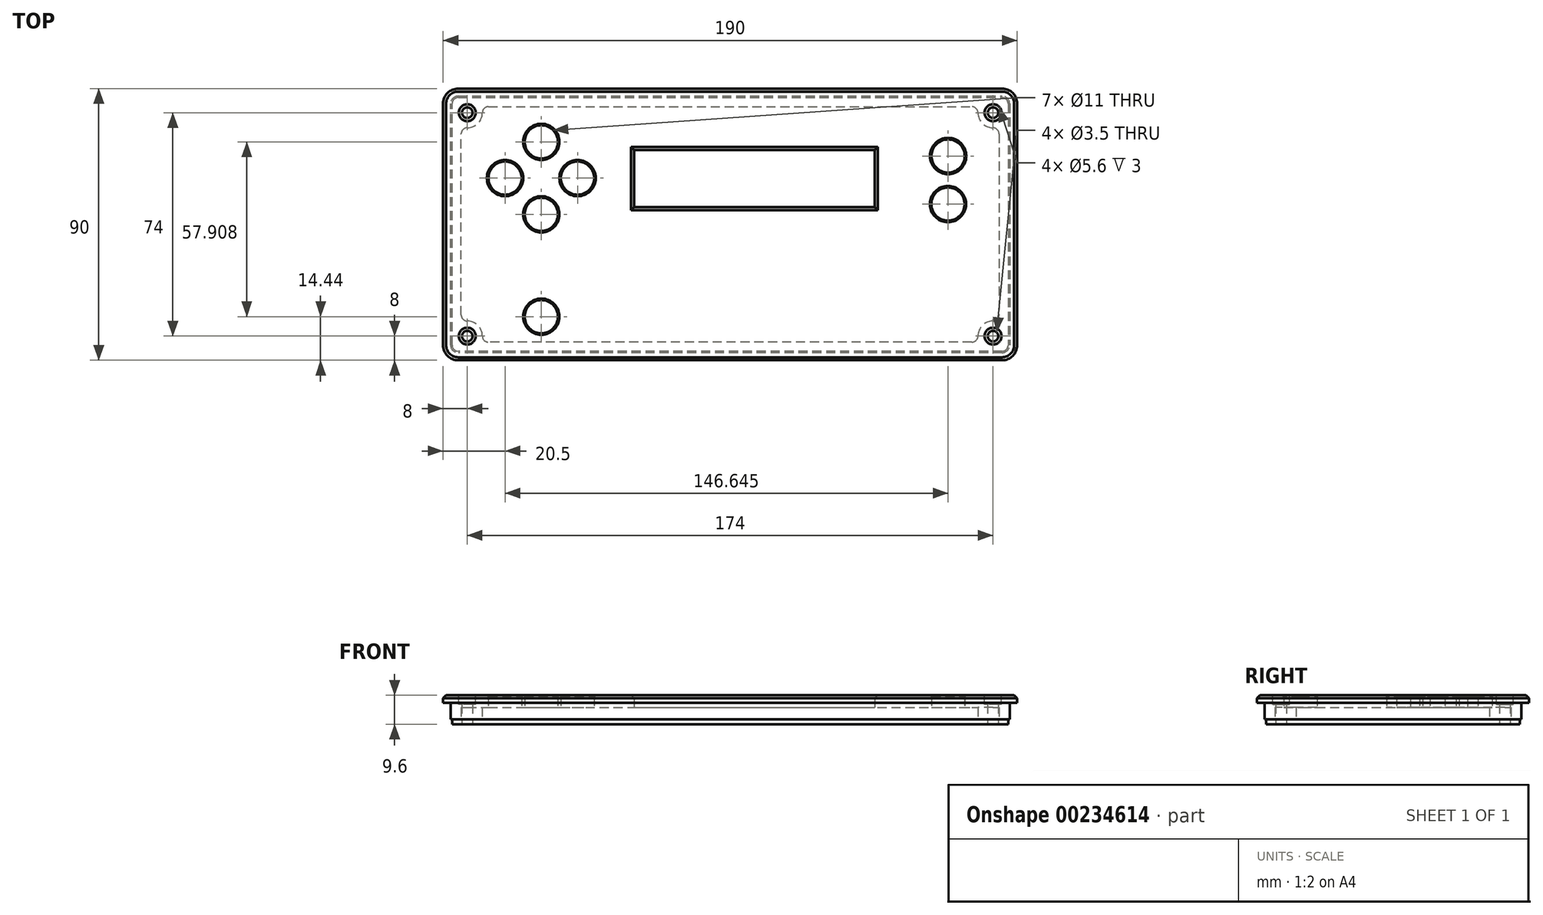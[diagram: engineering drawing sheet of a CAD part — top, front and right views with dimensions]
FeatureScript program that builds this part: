
annotation { "Feature Type Name" : "Feature", "Feature Type Description" : "" }
export const myFeature = defineFeature(function(context is Context, id is Id, definition is map)
    precondition{}
    {
        {
            var Q0;
            Q0=qCreatedBy(makeId("Top.planeOp"),FACE);
            var sketch = newSketch(context, id + "F0", { "sketchPlane" : qUnion([Q0])});
            skLineSegment(sketch, "E0.bottom", {"start": v(95, 45) * mm, "end": v(-95, 45) * mm});
            skLineSegment(sketch, "E0.top", {"start": v(95, -45) * mm, "end": v(-95, -45) * mm});
            skLineSegment(sketch, "E0.left", {"start": v(95, 45) * mm, "end": v(95, -45) * mm});
            skLineSegment(sketch, "E0.right", {"start": v(-95, 45) * mm, "end": v(-95, -45) * mm});
            skPoint(sketch, "E0.middle", {"position": v(0, 0) * mm});
            skCircle(sketch, "E1", {"center": v(-87, 37) * mm, "radius": 1.75 * mm});
            skLineSegment(sketch, "E2.bottom", {"start": v(47.83, 24.69) * mm, "end": v(-31.82, 24.69) * mm});
            skLineSegment(sketch, "E2.top", {"start": v(47.83, 5.74) * mm, "end": v(-31.82, 5.74) * mm});
            skLineSegment(sketch, "E2.left", {"start": v(47.83, 24.69) * mm, "end": v(47.83, 5.74) * mm});
            skLineSegment(sketch, "E2.right", {"start": v(-31.82, 24.69) * mm, "end": v(-31.82, 5.74) * mm});
            skCircle(sketch, "E3", {"center": v(-62.5, 27.35) * mm, "radius": 5.5 * mm});
            skCircle(sketch, "E4", {"center": v(-74.5, 15.35) * mm, "radius": 5.5 * mm});
            skCircle(sketch, "E5", {"center": v(-62.5, -30.56) * mm, "radius": 5.5 * mm});
            skCircle(sketch, "E6", {"center": v(72.14, 22.67) * mm, "radius": 5.5 * mm});
            skCircle(sketch, "E7", {"center": v(72.1, 6.74) * mm, "radius": 5.5 * mm});
            skLineSegment(sketch, "E8", {"start": v(-62.5, 27.35) * mm, "end": v(-62.5, -39.93) * mm, "construction": true});
            skLineSegment(sketch, "E9", {"start": v(-74.5, 15.35) * mm, "end": v(-45.37, 15.35) * mm, "construction": true});
            skCircle(sketch, "E10.MirrorC", {"center": v(-62.5, 3.35) * mm, "radius": 5.5 * mm});
            skCircle(sketch, "E11.MirrorC", {"center": v(-50.5, 15.35) * mm, "radius": 5.5 * mm});
            skLineSegment(sketch, "E12", {"start": v(72.14, 22.67) * mm, "end": v(72.1, 6.74) * mm, "construction": true});
            skCircle(sketch, "E13.MirrorC", {"center": v(87, 37) * mm, "radius": 1.75 * mm});
            skCircle(sketch, "E14.MirrorC", {"center": v(-87, -37) * mm, "radius": 1.75 * mm});
            skCircle(sketch, "E15.MirrorC", {"center": v(87, -37) * mm, "radius": 1.75 * mm});
            skSolve(sketch);
        }
        {
            var Q0;
            Q0 = qSketchRegion(id + "F0", true);
            extrude(context, id + "F1", {"entities" : qUnion([Q0]), "depth" : 8 * mm});
        }
        {
            var Q0;
            Q0=makeQuery(id+"F1.opExtrude","SWEPT_EDGE",EDGE,{"disambiguationData":[OSD([sQuery(id+"F0.wireOp",EDGE,"E0.bottom"),sQuery(id+"F0.wireOp",EDGE,"E0.right")])]});
            var Q1;
            Q1=makeQuery(id+"F1.opExtrude","SWEPT_EDGE",EDGE,{"disambiguationData":[OSD([sQuery(id+"F0.wireOp",EDGE,"E0.top"),sQuery(id+"F0.wireOp",EDGE,"E0.right")])]});
            var Q2;
            Q2=makeQuery(id+"F1.opExtrude","SWEPT_EDGE",EDGE,{"disambiguationData":[OSD([sQuery(id+"F0.wireOp",EDGE,"E0.top"),sQuery(id+"F0.wireOp",EDGE,"E0.left")])]});
            var Q3;
            Q3=makeQuery(id+"F1.opExtrude","SWEPT_EDGE",EDGE,{"disambiguationData":[OSD([sQuery(id+"F0.wireOp",EDGE,"E0.bottom"),sQuery(id+"F0.wireOp",EDGE,"E0.left")])]});
            fillet(context, id + "F2", {"entities" : qUnion([Q0, Q1, Q2, Q3]), "radius" : 5 * mm, "tangentPropagation" : true, "allowEdgeOverflow" : false});
        }
        {
            var Q0;
            Q0=makeQuery(id+"F1.opExtrude","CAP_FACE",FACE,{"disambiguationData":[OSD([sQuery(id+"F0.wireOp",EDGE,"E0.bottom"),sQuery(id+"F0.wireOp",EDGE,"E0.top"),sQuery(id+"F0.wireOp",EDGE,"E0.left"),sQuery(id+"F0.wireOp",EDGE,"E0.right"),sQuery(id+"F0.wireOp",EDGE,"E1"),sQuery(id+"F0.wireOp",EDGE,"E2.bottom"),sQuery(id+"F0.wireOp",EDGE,"E2.top"),sQuery(id+"F0.wireOp",EDGE,"E2.left"),sQuery(id+"F0.wireOp",EDGE,"E2.right"),sQuery(id+"F0.wireOp",EDGE,"E3"),sQuery(id+"F0.wireOp",EDGE,"E4"),sQuery(id+"F0.wireOp",EDGE,"E5"),sQuery(id+"F0.wireOp",EDGE,"E6"),sQuery(id+"F0.wireOp",EDGE,"E7"),sQuery(id+"F0.wireOp",EDGE,"E10.MirrorC"),sQuery(id+"F0.wireOp",EDGE,"E11.MirrorC"),sQuery(id+"F0.wireOp",EDGE,"E13.MirrorC"),sQuery(id+"F0.wireOp",EDGE,"E14.MirrorC"),sQuery(id+"F0.wireOp",EDGE,"E15.MirrorC")])],"isStart":true});
            var sketch = newSketch(context, id + "F3", { "sketchPlane" : qUnion([Q0])});
            skLineSegment(sketch, "E16.0", {"start": v(89, -32.42) * mm, "end": v(89, 32.42) * mm});
            skLineSegment(sketch, "E16.1", {"start": v(-82.42, -39) * mm, "end": v(82.42, -39) * mm});
            skLineSegment(sketch, "E16.3", {"start": v(82.42, 39) * mm, "end": v(-82.42, 39) * mm});
            skLineSegment(sketch, "E17.trimOffspring", {"start": v(-89, 32.42) * mm, "end": v(-89, -32.42) * mm});
            skArc(sketch, "E18", {"start": v(-89, 32.42) * mm, "mid": v(-83.46, 33.46) * mm, "end": v(-82.42, 39) * mm});
            skArc(sketch, "E19.MirrorC", {"start": v(89, 32.42) * mm, "mid": v(83.46, 33.46) * mm, "end": v(82.42, 39) * mm});
            skArc(sketch, "E20.MirrorC", {"start": v(-89, -32.42) * mm, "mid": v(-83.46, -33.46) * mm, "end": v(-82.42, -39) * mm});
            skArc(sketch, "E21.MirrorC", {"start": v(89, -32.42) * mm, "mid": v(83.46, -33.46) * mm, "end": v(82.42, -39) * mm});
            skPoint(sketch, "E22.orphan", {"position": v(-85.53, -39) * mm});
            skPoint(sketch, "E23.orphan", {"position": v(-89, -35.53) * mm});
            skPoint(sketch, "E24.orphan", {"position": v(-89, 35.53) * mm});
            skPoint(sketch, "E25.orphan", {"position": v(-85.53, 39) * mm});
            skPoint(sketch, "E26.orphan", {"position": v(89, 35.53) * mm});
            skPoint(sketch, "E27.orphan", {"position": v(85.53, 39) * mm});
            skPoint(sketch, "E28.orphan", {"position": v(89, -35.53) * mm});
            skPoint(sketch, "E29.orphan", {"position": v(85.53, -39) * mm});
            skSolve(sketch);
        }
        {
            var Q0;
            Q0 = qSketchRegion(id + "F3", true);
            extrude(context, id + "F4", {"entities" : qUnion([Q0]), "operationType" : NewBodyOperationType.REMOVE, "oppositeDirection" : true, "depth" : 4 * mm});
        }
        {
            var Q0;
            Q0=makeQuery(id+"F1.opExtrude","CAP_EDGE",EDGE,{"disambiguationData":[OSD([sQuery(id+"F0.wireOp",EDGE,"E3")])],"isStart":false});
            var Q1;
            Q1=makeQuery(id+"F1.opExtrude","CAP_EDGE",EDGE,{"disambiguationData":[OSD([sQuery(id+"F0.wireOp",EDGE,"E11.MirrorC")])],"isStart":false});
            var Q2;
            Q2=makeQuery(id+"F1.opExtrude","CAP_EDGE",EDGE,{"disambiguationData":[OSD([sQuery(id+"F0.wireOp",EDGE,"E4")])],"isStart":false});
            var Q3;
            Q3=makeQuery(id+"F1.opExtrude","CAP_EDGE",EDGE,{"disambiguationData":[OSD([sQuery(id+"F0.wireOp",EDGE,"E10.MirrorC")])],"isStart":false});
            var Q4;
            Q4=makeQuery(id+"F1.opExtrude","CAP_EDGE",EDGE,{"disambiguationData":[OSD([sQuery(id+"F0.wireOp",EDGE,"E5")])],"isStart":false});
            var Q5;
            Q5=makeQuery(id+"F1.opExtrude","CAP_EDGE",EDGE,{"disambiguationData":[OSD([sQuery(id+"F0.wireOp",EDGE,"E6")])],"isStart":false});
            var Q6;
            Q6=makeQuery(id+"F1.opExtrude","CAP_EDGE",EDGE,{"disambiguationData":[OSD([sQuery(id+"F0.wireOp",EDGE,"E7")])],"isStart":false});
            chamfer(context, id + "F5", {"entities" : qUnion([Q0, Q1, Q2, Q3, Q4, Q5, Q6]), "width" : .5 * mm, "tangentPropagation" : true});
        }
        {
            var Q0;
            Q0=makeQuery(id+"F1.opExtrude","CAP_EDGE",EDGE,{"disambiguationData":[OSD([sQuery(id+"F0.wireOp",EDGE,"E2.bottom")])],"isStart":false});
            var Q1;
            Q1=makeQuery(id+"F1.opExtrude","CAP_EDGE",EDGE,{"disambiguationData":[OSD([sQuery(id+"F0.wireOp",EDGE,"E2.right")])],"isStart":false});
            var Q2;
            Q2=makeQuery(id+"F1.opExtrude","CAP_EDGE",EDGE,{"disambiguationData":[OSD([sQuery(id+"F0.wireOp",EDGE,"E2.left")])],"isStart":false});
            var Q3;
            Q3=makeQuery(id+"F1.opExtrude","CAP_EDGE",EDGE,{"disambiguationData":[OSD([sQuery(id+"F0.wireOp",EDGE,"E2.top")])],"isStart":false});
            var Q4;
            Q4=makeQuery(id+"F1.opExtrude","CAP_EDGE",EDGE,{"disambiguationData":[OSD([sQuery(id+"F0.wireOp",EDGE,"E0.bottom")])],"isStart":false});
            chamfer(context, id + "F6", {"entities" : qUnion([Q0, Q1, Q2, Q3, Q4]), "width" : 1 * mm, "tangentPropagation" : true});
        }
        {
            var Q0;
            Q0=makeQuery(id+"F4.boolean.opBoolean","COPY",EDGE,{"derivedFrom":makeQuery(id+"F4.opExtrude","SWEPT_EDGE",EDGE,{"disambiguationData":[OSD([sQuery(id+"F3.wireOp",EDGE,"E17.trimOffspring"),sQuery(id+"F3.wireOp",EDGE,"E18")])]})});
            var Q1;
            Q1=makeQuery(id+"F4.boolean.opBoolean","COPY",EDGE,{"derivedFrom":makeQuery(id+"F4.opExtrude","SWEPT_EDGE",EDGE,{"disambiguationData":[OSD([sQuery(id+"F3.wireOp",EDGE,"E16.3"),sQuery(id+"F3.wireOp",EDGE,"E18")])]})});
            var Q2;
            Q2=makeQuery(id+"F4.boolean.opBoolean","COPY",EDGE,{"derivedFrom":makeQuery(id+"F4.opExtrude","SWEPT_EDGE",EDGE,{"disambiguationData":[OSD([sQuery(id+"F3.wireOp",EDGE,"E16.3"),sQuery(id+"F3.wireOp",EDGE,"E19.MirrorC")])]})});
            var Q3;
            Q3=makeQuery(id+"F4.boolean.opBoolean","COPY",EDGE,{"derivedFrom":makeQuery(id+"F4.opExtrude","SWEPT_EDGE",EDGE,{"disambiguationData":[OSD([sQuery(id+"F3.wireOp",EDGE,"E16.0"),sQuery(id+"F3.wireOp",EDGE,"E19.MirrorC")])]})});
            var Q4;
            Q4=makeQuery(id+"F4.boolean.opBoolean","COPY",EDGE,{"derivedFrom":makeQuery(id+"F4.opExtrude","SWEPT_EDGE",EDGE,{"disambiguationData":[OSD([sQuery(id+"F3.wireOp",EDGE,"E16.0"),sQuery(id+"F3.wireOp",EDGE,"E21.MirrorC")])]})});
            var Q5;
            Q5=makeQuery(id+"F4.boolean.opBoolean","COPY",EDGE,{"derivedFrom":makeQuery(id+"F4.opExtrude","SWEPT_EDGE",EDGE,{"disambiguationData":[OSD([sQuery(id+"F3.wireOp",EDGE,"E16.1"),sQuery(id+"F3.wireOp",EDGE,"E21.MirrorC")])]})});
            var Q6;
            Q6=makeQuery(id+"F4.boolean.opBoolean","COPY",EDGE,{"derivedFrom":makeQuery(id+"F4.opExtrude","SWEPT_EDGE",EDGE,{"disambiguationData":[OSD([sQuery(id+"F3.wireOp",EDGE,"E16.1"),sQuery(id+"F3.wireOp",EDGE,"E20.MirrorC")])]})});
            var Q7;
            Q7=makeQuery(id+"F4.boolean.opBoolean","COPY",EDGE,{"derivedFrom":makeQuery(id+"F4.opExtrude","SWEPT_EDGE",EDGE,{"disambiguationData":[OSD([sQuery(id+"F3.wireOp",EDGE,"E17.trimOffspring"),sQuery(id+"F3.wireOp",EDGE,"E20.MirrorC")])]})});
            fillet(context, id + "F7", {"entities" : qUnion([Q0, Q1, Q2, Q3, Q4, Q5, Q6, Q7]), "radius" : 2 * mm, "tangentPropagation" : true, "allowEdgeOverflow" : false});
        }
        {
            var Q0;
            Q0=makeQuery(id+"F1.opExtrude","CAP_FACE",FACE,{"disambiguationData":[OSD([sQuery(id+"F0.wireOp",EDGE,"E0.bottom"),sQuery(id+"F0.wireOp",EDGE,"E0.top"),sQuery(id+"F0.wireOp",EDGE,"E0.left"),sQuery(id+"F0.wireOp",EDGE,"E0.right"),sQuery(id+"F0.wireOp",EDGE,"E1"),sQuery(id+"F0.wireOp",EDGE,"E2.bottom"),sQuery(id+"F0.wireOp",EDGE,"E2.top"),sQuery(id+"F0.wireOp",EDGE,"E2.left"),sQuery(id+"F0.wireOp",EDGE,"E2.right"),sQuery(id+"F0.wireOp",EDGE,"E3"),sQuery(id+"F0.wireOp",EDGE,"E4"),sQuery(id+"F0.wireOp",EDGE,"E5"),sQuery(id+"F0.wireOp",EDGE,"E6"),sQuery(id+"F0.wireOp",EDGE,"E7"),sQuery(id+"F0.wireOp",EDGE,"E10.MirrorC"),sQuery(id+"F0.wireOp",EDGE,"E11.MirrorC"),sQuery(id+"F0.wireOp",EDGE,"E13.MirrorC"),sQuery(id+"F0.wireOp",EDGE,"E14.MirrorC"),sQuery(id+"F0.wireOp",EDGE,"E15.MirrorC")])],"isStart":false});
            var sketch = newSketch(context, id + "F8", { "sketchPlane" : qUnion([Q0])});
            skCircle(sketch, "E30", {"center": v(-87, 37) * mm, "radius": 2.8 * mm});
            skCircle(sketch, "E31.MirrorC", {"center": v(87, 37) * mm, "radius": 2.8 * mm});
            skCircle(sketch, "E32.MirrorC", {"center": v(-87, -37) * mm, "radius": 2.8 * mm});
            skCircle(sketch, "E33.MirrorC", {"center": v(87, -37) * mm, "radius": 2.8 * mm});
            skSolve(sketch);
        }
        {
            var Q0;
            Q0 = qSketchRegion(id + "F8", true);
            extrude(context, id + "F9", {"entities" : qUnion([Q0]), "operationType" : NewBodyOperationType.REMOVE, "oppositeDirection" : true, "depth" : 3 * mm});
        }
        {
            var Q0;
            Q0=makeQuery(id+"F1.opExtrude","CAP_FACE",FACE,{"disambiguationData":[OSD([sQuery(id+"F0.wireOp",EDGE,"E0.bottom"),sQuery(id+"F0.wireOp",EDGE,"E0.top"),sQuery(id+"F0.wireOp",EDGE,"E0.left"),sQuery(id+"F0.wireOp",EDGE,"E0.right"),sQuery(id+"F0.wireOp",EDGE,"E1"),sQuery(id+"F0.wireOp",EDGE,"E2.bottom"),sQuery(id+"F0.wireOp",EDGE,"E2.top"),sQuery(id+"F0.wireOp",EDGE,"E2.left"),sQuery(id+"F0.wireOp",EDGE,"E2.right"),sQuery(id+"F0.wireOp",EDGE,"E3"),sQuery(id+"F0.wireOp",EDGE,"E4"),sQuery(id+"F0.wireOp",EDGE,"E5"),sQuery(id+"F0.wireOp",EDGE,"E6"),sQuery(id+"F0.wireOp",EDGE,"E7"),sQuery(id+"F0.wireOp",EDGE,"E10.MirrorC"),sQuery(id+"F0.wireOp",EDGE,"E11.MirrorC"),sQuery(id+"F0.wireOp",EDGE,"E13.MirrorC"),sQuery(id+"F0.wireOp",EDGE,"E14.MirrorC"),sQuery(id+"F0.wireOp",EDGE,"E15.MirrorC")])],"isStart":true});
            var sketch = newSketch(context, id + "F10", { "sketchPlane" : qUnion([Q0])});
            skArc(sketch, "E34.0", {"start": v(90, -45) * mm, "mid": v(93.54, -43.54) * mm, "end": v(95, -40) * mm});
            skLineSegment(sketch, "E34.1", {"start": v(-90, -45) * mm, "end": v(90, -45) * mm});
            skLineSegment(sketch, "E34.2", {"start": v(95, -40) * mm, "end": v(95, 40) * mm});
            skArc(sketch, "E34.3", {"start": v(-95, -40) * mm, "mid": v(-93.54, -43.54) * mm, "end": v(-90, -45) * mm});
            skArc(sketch, "E34.4", {"start": v(95, 40) * mm, "mid": v(93.54, 43.54) * mm, "end": v(90, 45) * mm});
            skLineSegment(sketch, "E34.5", {"start": v(90, 45) * mm, "end": v(-90, 45) * mm});
            skArc(sketch, "E34.6", {"start": v(-90, 45) * mm, "mid": v(-93.54, 43.54) * mm, "end": v(-95, 40) * mm});
            skLineSegment(sketch, "E34.7", {"start": v(-95, 40) * mm, "end": v(-95, -40) * mm});
            skArc(sketch, "E35.0", {"start": v(90, -42.5) * mm, "mid": v(91.77, -41.77) * mm, "end": v(92.5, -40) * mm});
            skLineSegment(sketch, "E35.1", {"start": v(-90, -42.5) * mm, "end": v(90, -42.5) * mm});
            skLineSegment(sketch, "E35.2", {"start": v(92.5, -40) * mm, "end": v(92.5, 40) * mm});
            skArc(sketch, "E35.3", {"start": v(-92.5, -40) * mm, "mid": v(-91.77, -41.77) * mm, "end": v(-90, -42.5) * mm});
            skArc(sketch, "E35.4", {"start": v(92.5, 40) * mm, "mid": v(91.77, 41.77) * mm, "end": v(90, 42.5) * mm});
            skLineSegment(sketch, "E35.5", {"start": v(90, 42.5) * mm, "end": v(-90, 42.5) * mm});
            skArc(sketch, "E35.6", {"start": v(-90, 42.5) * mm, "mid": v(-91.77, 41.77) * mm, "end": v(-92.5, 40) * mm});
            skLineSegment(sketch, "E35.7", {"start": v(-92.5, 40) * mm, "end": v(-92.5, -40) * mm});
            skSolve(sketch);
        }
        {
            var Q0;
            Q0 = qSketchRegion(id + "F10", true);
            extrude(context, id + "F11", {"entities" : qUnion([Q0]), "operationType" : NewBodyOperationType.REMOVE, "oppositeDirection" : true, "depth" : 5.5 * mm});
        }
        {
            var Q0;
            Q0=makeQuery(id+"F1.opExtrude","CAP_FACE",FACE,{"disambiguationData":[OSD([sQuery(id+"F0.wireOp",EDGE,"E0.bottom"),sQuery(id+"F0.wireOp",EDGE,"E0.top"),sQuery(id+"F0.wireOp",EDGE,"E0.left"),sQuery(id+"F0.wireOp",EDGE,"E0.right"),sQuery(id+"F0.wireOp",EDGE,"E1"),sQuery(id+"F0.wireOp",EDGE,"E2.bottom"),sQuery(id+"F0.wireOp",EDGE,"E2.top"),sQuery(id+"F0.wireOp",EDGE,"E2.left"),sQuery(id+"F0.wireOp",EDGE,"E2.right"),sQuery(id+"F0.wireOp",EDGE,"E3"),sQuery(id+"F0.wireOp",EDGE,"E4"),sQuery(id+"F0.wireOp",EDGE,"E5"),sQuery(id+"F0.wireOp",EDGE,"E6"),sQuery(id+"F0.wireOp",EDGE,"E7"),sQuery(id+"F0.wireOp",EDGE,"E10.MirrorC"),sQuery(id+"F0.wireOp",EDGE,"E11.MirrorC"),sQuery(id+"F0.wireOp",EDGE,"E13.MirrorC"),sQuery(id+"F0.wireOp",EDGE,"E14.MirrorC"),sQuery(id+"F0.wireOp",EDGE,"E15.MirrorC")])],"isStart":true});
            var sketch = newSketch(context, id + "F12", { "sketchPlane" : qUnion([Q0])});
            skArc(sketch, "E36.0", {"start": v(-90, 42) * mm, "mid": v(-91.41, 41.41) * mm, "end": v(-92, 40) * mm});
            skLineSegment(sketch, "E36.1", {"start": v(90, 42) * mm, "end": v(-90, 42) * mm});
            skLineSegment(sketch, "E36.2", {"start": v(-92, 40) * mm, "end": v(-92, -40) * mm});
            skArc(sketch, "E36.3", {"start": v(92, 40) * mm, "mid": v(91.41, 41.41) * mm, "end": v(90, 42) * mm});
            skArc(sketch, "E36.4", {"start": v(-92, -40) * mm, "mid": v(-91.41, -41.41) * mm, "end": v(-90, -42) * mm});
            skLineSegment(sketch, "E36.5", {"start": v(-90, -42) * mm, "end": v(90, -42) * mm});
            skArc(sketch, "E36.6", {"start": v(90, -42) * mm, "mid": v(91.41, -41.41) * mm, "end": v(92, -40) * mm});
            skLineSegment(sketch, "E36.7", {"start": v(92, -40) * mm, "end": v(92, 40) * mm});
            skCircle(sketch, "E37.0", {"center": v(87, -37) * mm, "radius": 1.75 * mm});
            skCircle(sketch, "E38.MirrorC", {"center": v(-87, -37) * mm, "radius": 1.75 * mm});
            skCircle(sketch, "E39.MirrorC", {"center": v(87, 37) * mm, "radius": 1.75 * mm});
            skCircle(sketch, "E40.MirrorC", {"center": v(-87, 37) * mm, "radius": 1.75 * mm});
            skSolve(sketch);
        }
        {
            var Q0;
            Q0 = qSketchRegion(id + "F12", true);
            extrude(context, id + "F13", {"entities" : qUnion([Q0]), "operationType" : NewBodyOperationType.ADD, "depth" : 1.6 * mm});
        }
    });
